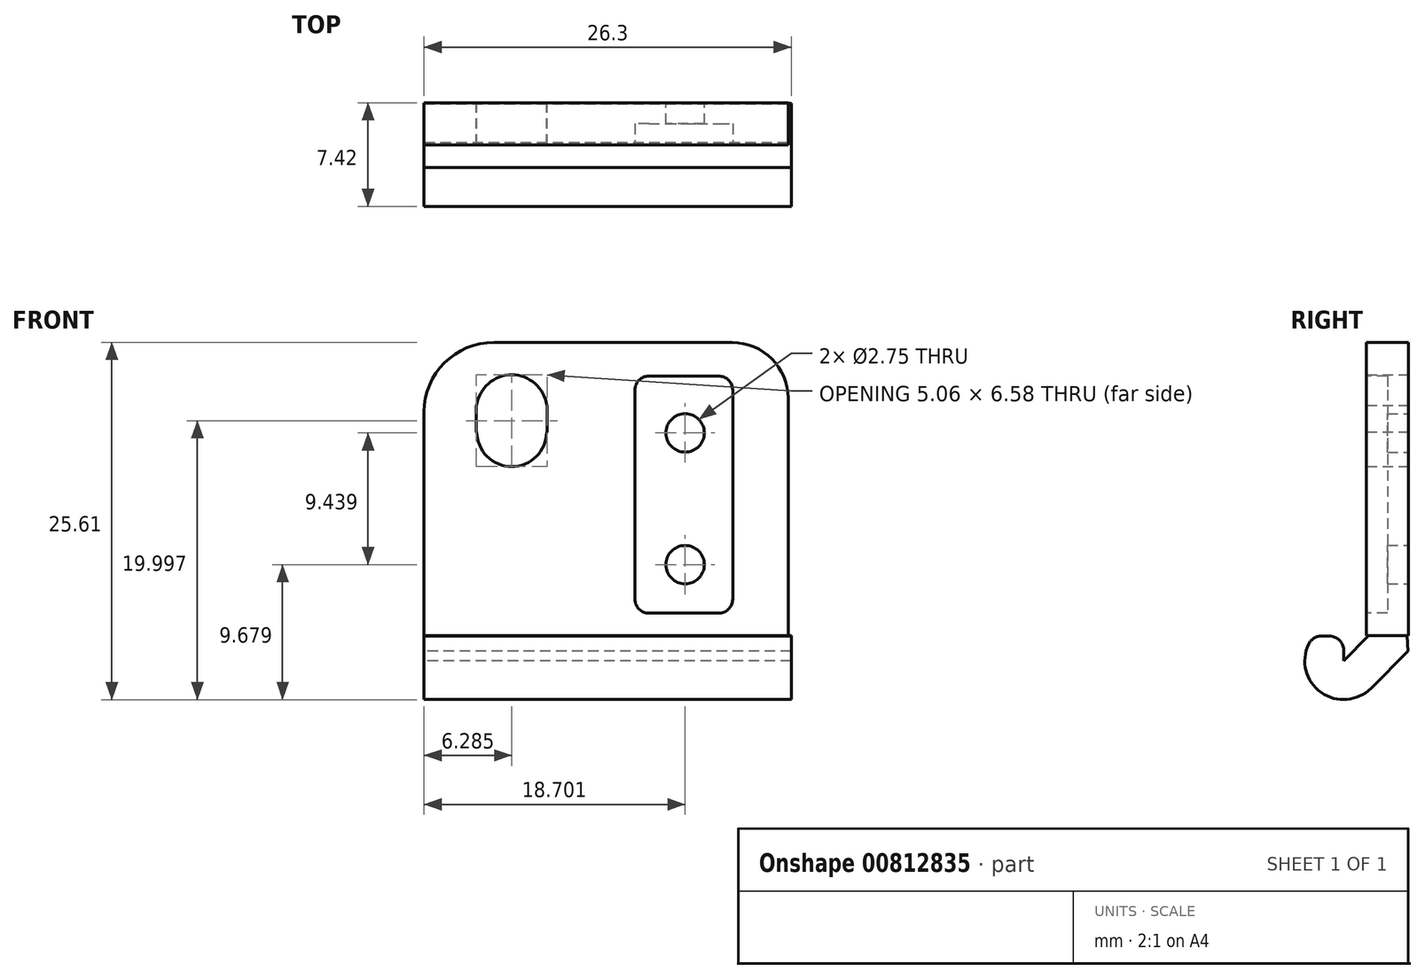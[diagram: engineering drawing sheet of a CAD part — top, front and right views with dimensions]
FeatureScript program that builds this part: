
annotation { "Feature Type Name" : "Feature", "Feature Type Description" : "" }
export const myFeature = defineFeature(function(context is Context, id is Id, definition is map)
    precondition{}
    {
        {
            var Q0;
            Q0=qCreatedBy(makeId("Front.planeOp"),FACE);
            var sketch = newSketch(context, id + "F0", { "sketchPlane" : qUnion([Q0])});
            skLineSegment(sketch, "E0.bottom", {"start": v(-7.99, 12.92) * mm, "end": v(9.09, 12.92) * mm});
            skLineSegment(sketch, "E0.top", {"start": v(-12.45, -8.12) * mm, "end": v(13.09, -8.12) * mm});
            skLineSegment(sketch, "E0.right", {"start": v(13.09, 8.92) * mm, "end": v(13.09, -8.12) * mm});
            skLineSegment(sketch, "E1", {"start": v(-12.45, -8.12) * mm, "end": v(-12.99, -8.12) * mm});
            skLineSegment(sketch, "E2", {"start": v(-12.99, -8.12) * mm, "end": v(-12.99, 7.92) * mm});
            skLineSegment(sketch, "E3", {"start": v(-12.99, 12.86) * mm, "end": v(-12.45, 12.92) * mm});
            skArc(sketch, "E4.filletArc", {"start": v(-7.99, 12.92) * mm, "mid": v(-11.52, 11.45) * mm, "end": v(-12.99, 7.92) * mm});
            skPoint(sketch, "E5.visualSharp", {"position": v(13.09, 12.92) * mm});
            skArc(sketch, "E5.filletArc", {"start": v(13.09, 8.92) * mm, "mid": v(11.92, 11.74) * mm, "end": v(9.09, 12.92) * mm});
            skCircle(sketch, "E6", {"center": v(5.71, 6.43) * mm, "radius": 1.38 * mm});
            skLineSegment(sketch, "E7.bottom", {"start": v(-9.24, 8.4) * mm, "end": v(-9.21, 8.4) * mm});
            skLineSegment(sketch, "E7.top", {"start": v(-9.24, 6.52) * mm, "end": v(-9.2, 6.52) * mm});
            skLineSegment(sketch, "E7.left", {"start": v(-9.24, 8.4) * mm, "end": v(-9.24, 6.52) * mm});
            skLineSegment(sketch, "E7.right", {"start": v(-4.17, 8.4) * mm, "end": v(-4.17, 6.52) * mm});
            skPoint(sketch, "E8", {"position": v(-6.7, 8.4) * mm});
            skArc(sketch, "E9.trimOffspring", {"start": v(-4.17, 8.07) * mm, "mid": v(-6.7, 10.6) * mm, "end": v(-9.24, 8.07) * mm});
            skLineSegment(sketch, "E10.trimOffspring", {"start": v(-4.2, 8.4) * mm, "end": v(-4.17, 8.4) * mm});
            skArc(sketch, "E11", {"start": v(-9.2, 6.52) * mm, "mid": v(-6.7, 4.02) * mm, "end": v(-4.2, 6.52) * mm});
            skLineSegment(sketch, "E12.trimOffspring", {"start": v(-4.2, 6.52) * mm, "end": v(-4.17, 6.52) * mm});
            skCircle(sketch, "E13", {"center": v(5.71, -3.01) * mm, "radius": 1.38 * mm});
            skSolve(sketch);
        }
        {
            var Q0;
            Q0 = qSketchRegion(id + "F0", true);
            extrude(context, id + "F1", {"entities" : qUnion([Q0]), "depth" : 3 * mm, "offsetDistance" : 25 * mm});
        }
        {
            var Q0;
            Q0=makeQuery(id+"F1.opExtrude","CAP_FACE",FACE,{"disambiguationData":[OSD([sQuery(id+"F0.wireOp",EDGE,"E0.bottom"),sQuery(id+"F0.wireOp",EDGE,"E0.top"),sQuery(id+"F0.wireOp",EDGE,"E0.right"),sQuery(id+"F0.wireOp",EDGE,"E1"),sQuery(id+"F0.wireOp",EDGE,"E2"),sQuery(id+"F0.wireOp",EDGE,"E4.filletArc"),sQuery(id+"F0.wireOp",EDGE,"E5.filletArc"),sQuery(id+"F0.wireOp",EDGE,"E6"),sQuery(id+"F0.wireOp",EDGE,"E7.bottom"),sQuery(id+"F0.wireOp",EDGE,"E7.top"),sQuery(id+"F0.wireOp",EDGE,"E7.left"),sQuery(id+"F0.wireOp",EDGE,"E7.right"),sQuery(id+"F0.wireOp",EDGE,"E9.trimOffspring"),sQuery(id+"F0.wireOp",EDGE,"E10.trimOffspring"),sQuery(id+"F0.wireOp",EDGE,"E11"),sQuery(id+"F0.wireOp",EDGE,"E12.trimOffspring"),sQuery(id+"F0.wireOp",EDGE,"E13")])],"isStart":false});
            var sketch = newSketch(context, id + "F2", { "sketchPlane" : qUnion([Q0])});
            skLineSegment(sketch, "E14.bottom", {"start": v(3.12, 10.5) * mm, "end": v(8.12, 10.5) * mm});
            skLineSegment(sketch, "E14.top", {"start": v(3.12, -6.5) * mm, "end": v(8.12, -6.5) * mm});
            skLineSegment(sketch, "E14.left", {"start": v(2.12, 9.5) * mm, "end": v(2.12, -5.5) * mm});
            skLineSegment(sketch, "E14.right", {"start": v(9.12, 9.5) * mm, "end": v(9.12, -5.5) * mm});
            skPoint(sketch, "E15.visualSharp", {"position": v(2.12, 10.5) * mm});
            skArc(sketch, "E15.filletArc", {"start": v(3.12, 10.5) * mm, "mid": v(2.41, 10.21) * mm, "end": v(2.12, 9.5) * mm});
            skPoint(sketch, "E16.visualSharp", {"position": v(9.12, 10.5) * mm});
            skArc(sketch, "E16.filletArc", {"start": v(9.12, 9.5) * mm, "mid": v(8.83, 10.21) * mm, "end": v(8.12, 10.5) * mm});
            skPoint(sketch, "E17.visualSharp", {"position": v(2.12, -6.5) * mm});
            skArc(sketch, "E17.filletArc", {"start": v(2.12, -5.5) * mm, "mid": v(2.41, -6.2) * mm, "end": v(3.12, -6.5) * mm});
            skPoint(sketch, "E18.visualSharp", {"position": v(9.12, -6.5) * mm});
            skArc(sketch, "E18.filletArc", {"start": v(8.12, -6.5) * mm, "mid": v(8.83, -6.2) * mm, "end": v(9.12, -5.5) * mm});
            skSolve(sketch);
        }
        {
            var Q0;
            Q0=makeQuery(id+"F2.imprint","IMPRINT",FACE,{"disambiguationData":[TD([[makeQuery(id+"F2.imprint","IMPRINT",EDGE,{"derivedFrom":sQuery(id+"F2.wireOp",EDGE,"E14.bottom")}),-1.0]])]});
            extrude(context, id + "F3", {"entities" : qUnion([Q0]), "operationType" : NewBodyOperationType.REMOVE, "oppositeDirection" : true, "depth" : 1.5 * mm, "offsetDistance" : 25 * mm});
        }
        {
            var Q0;
            Q0=makeQuery(id+"F1.opExtrude","SWEPT_FACE",FACE,{"disambiguationData":[OSD([sQuery(id+"F0.wireOp",EDGE,"E2")])]});
            var sketch = newSketch(context, id + "F4", { "sketchPlane" : qUnion([Q0])});
            skSolve(sketch);
        }
        {
            var Q0;
            {var subQ0=sQuery(id+"F0.wireOp",EDGE,"E2");Q0=makeQuery(id+"F4.imprint","IMPRINT",FACE,{"disambiguationData":[TD([[makeQuery(id+"F4.imprint","IMPRINT",EDGE,{"derivedFrom":makeQuery(id+"F1.opExtrude","CAP_EDGE",EDGE,{"disambiguationData":[OSD([subQ0])],"isStart":true})}),-1.0]])]});}
            var sketch = newSketch(context, id + "F5", { "sketchPlane" : qUnion([Q0])});
            skLineSegment(sketch, "E19", {"start": v(0.02, -9.2) * mm, "end": v(2.67, -11.87) * mm});
            skLineSegment(sketch, "E20", {"start": v(4.64, -9.9) * mm, "end": v(2.85, -8.1) * mm});
            skLineSegment(sketch, "E21", {"start": v(2.85, -8.1) * mm, "end": v(0.1, -8.1) * mm});
            skLineSegment(sketch, "E22", {"start": v(0.02, -9.2) * mm, "end": v(0.1, -8.1) * mm});
            skLineSegment(sketch, "E23", {"start": v(4.64, -9.9) * mm, "end": v(4.64, -9.14) * mm});
            skLineSegment(sketch, "E24", {"start": v(6.25, -8.14) * mm, "end": v(5.64, -8.14) * mm});
            skPoint(sketch, "E25.visualSharp", {"position": v(4.64, -8.14) * mm});
            skArc(sketch, "E25.filletArc", {"start": v(5.64, -8.14) * mm, "mid": v(4.94, -8.43) * mm, "end": v(4.64, -9.14) * mm});
            skPoint(sketch, "E26.visualSharp", {"position": v(7.25, -8.14) * mm});
            skArc(sketch, "E26.filletArc", {"start": v(7.25, -9.14) * mm, "mid": v(6.96, -8.43) * mm, "end": v(6.25, -8.14) * mm});
            skArc(sketch, "E27", {"start": v(2.67, -11.87) * mm, "mid": v(6.25, -12.18) * mm, "end": v(7.15, -8.7) * mm});
            skSolve(sketch);
        }
        {
            var Q0;
            Q0 = qSketchRegion(id + "F5", true);
            extrude(context, id + "F6", {"entities" : qUnion([Q0]), "operationType" : NewBodyOperationType.ADD, "oppositeDirection" : true, "depth" : 26.3 * mm, "offsetDistance" : 25 * mm});
        }
    });
